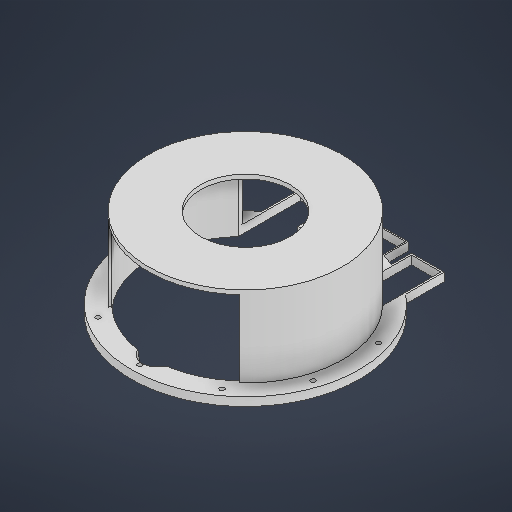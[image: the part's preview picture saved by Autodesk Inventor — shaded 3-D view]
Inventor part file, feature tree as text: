
AUTODESK INVENTOR PART (.ipt)
format: ipt  version: 2025 (Build 290162000, 162)  size: 363,008 bytes
history: native  units: in
note: dims shown in document units (in); Inventor stores cm internally (conversion verified against a paired STEP export)
features: extrude x8, sketch x7, plane x3
ambient origin geometry x8: Origin, YZ Plane, XZ Plane, XY Plane, X Axis, Y Axis, Z Axis, Center Point
bodies: Solid1 (feature_tree)
feature tree (18):
  sketch  "Sketch1"  dims[d5=0.0in d7=0.0in]
  extrude  "Extrusion1"  TaperAngle=0.0deg  [1 undecoded]
  extrude  "Extrusion2"  Depth=4.5276in
  extrude  "Extrusion7"  Depth=2.5591in
  sketch  "Sketch24"  dims[d237=0.0591in d238=2.564in]
  extrude  "Extrusion30"  Depth=2.564in
  extrude  "Extrusion31"  Depth=10.6299in
  extrude  "Extrusion32"  Depth=0.5433in
  extrude  "Extrusion34"  Depth=0.3937in
  sketch  "Sketch30"  dims[d242=2.7608in d243=0.5433in]
  plane  "Work Plane19"
  plane  "Work Plane22"
  extrude  "Extrusion36"  Depth=0.3937in
  sketch  "Sketch2"  dims[d18=0.0in d52=4.5276in]
  sketch  "Sketch Circular Pattern5"  dims[d234=0.0787in d235=2.5591in]
  sketch  "Sketch28"  dims[d240=0.8253in d241=10.6299in]
  plane  "Work Plane21"
  sketch  "Sketch31"  dims[d244=1.5298in d247=0.0787in d248=3.5433in d249=3.6614in d250=0.0in d251=3.6614in d252=0.0in d253=9.4488in d254=0.3937in d255=0.0in d264=9.8425in d265=0.2165in d266=3.937in d268=360.0deg d270=1.7955in d271=6.1024in d272=3.937in d273=4.1535in d274=0.0in d282=0.1598in d284=0.7851in d285=3.937in d286=1.4567in d287=2.0812in d288=0.0in d289=3.5039in d113=0.0197in d114=0.0344in d115=0.0197in d116=0.0344in d167=0.0197in d168=0.0344in d169=0.0197in d170=0.0344in d215=0.0197in d216=0.0344in d217=0.0197in d218=0.0344in d219=0.0in d220=0.0in d256=0.0197in d257=0.0344in]
note: 1 required parameter value undecoded (feature->parameter linkage not recoverable at this tier; creation-order binding heuristic only, values carry confidence <= 0.55)
